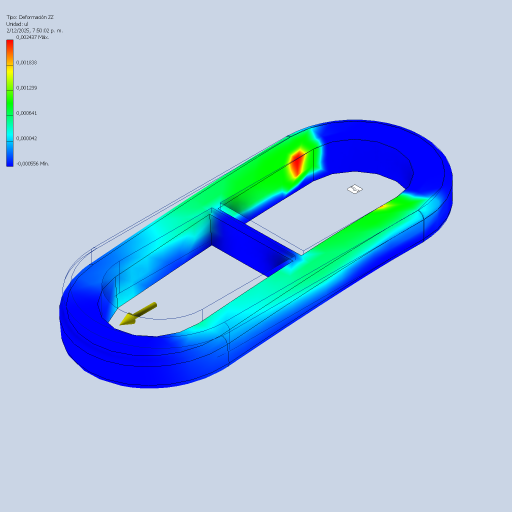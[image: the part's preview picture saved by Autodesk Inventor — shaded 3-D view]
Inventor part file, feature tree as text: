
AUTODESK INVENTOR PART (.ipt)
format: ipt  version: 2024 (Build 280153000, 153)  size: 225,792 bytes
history: native  units: mm
features: extrude x1, fillet x1, sketch x1
ambient origin geometry x8: Origin, YZ Plane, XZ Plane, XY Plane, X Axis, Y Axis, Z Axis, Center Point
bodies: Body1 (feature_tree)
feature tree (3):
  extrude  "Extrusión2"  Depth=10.0mm
  fillet  "Empalme1"  Radius=0.0mm
  sketch  "Boceto1"  dims[d1=50.0mm d3=10.0mm d6=0.0mm d9=1.5mm d10=10.0mm d11=0.0mm d12=2.0mm]
